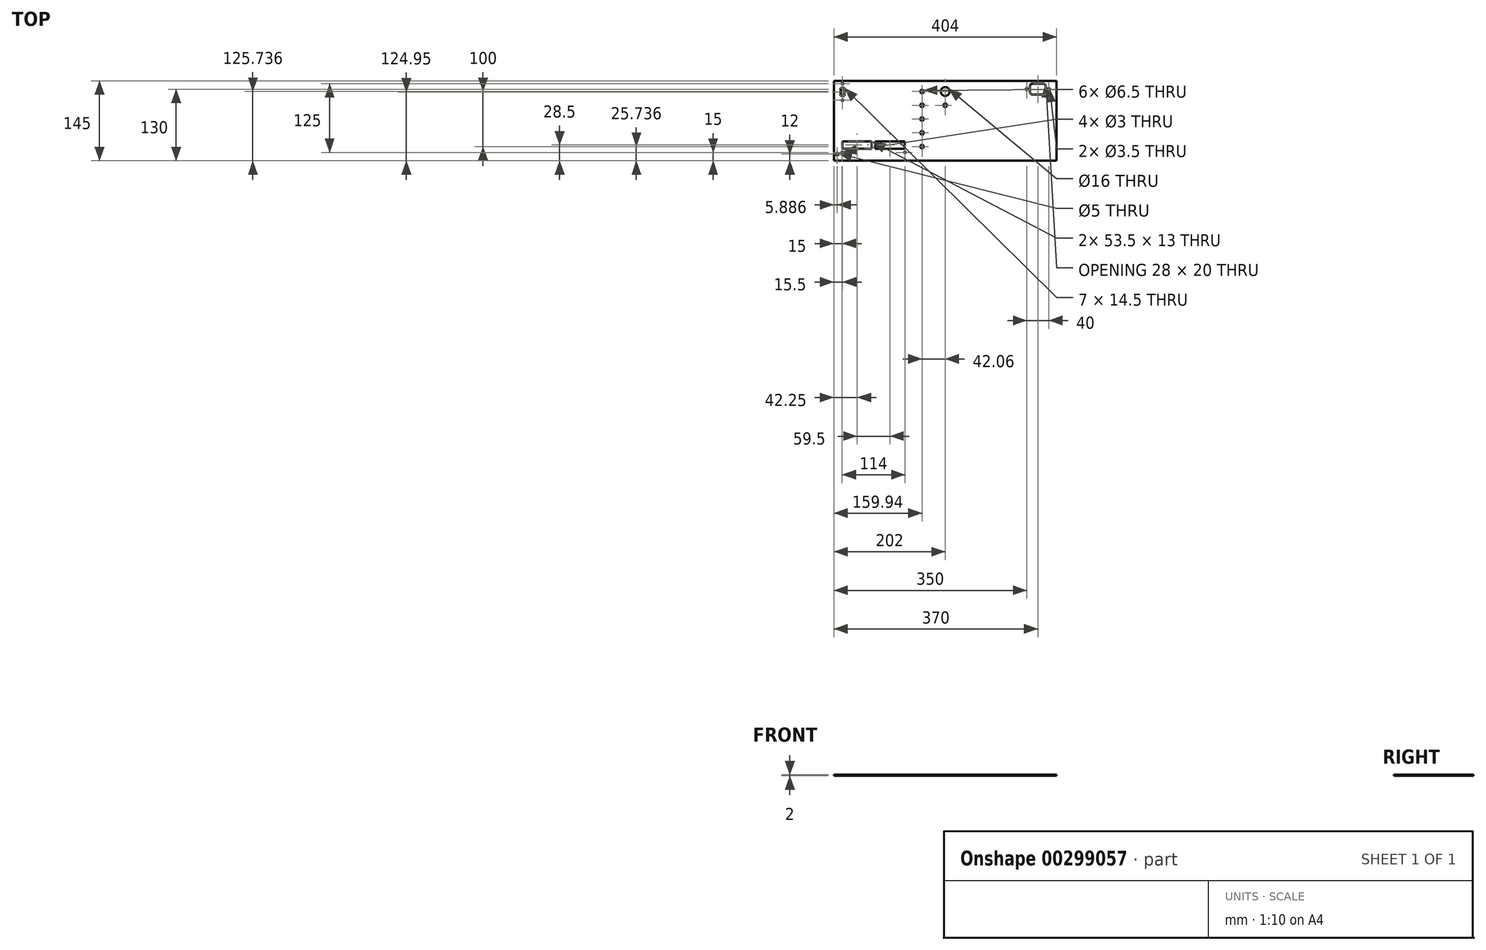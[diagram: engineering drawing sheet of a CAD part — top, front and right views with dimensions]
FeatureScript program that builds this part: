
annotation { "Feature Type Name" : "Feature", "Feature Type Description" : "" }
export const myFeature = defineFeature(function(context is Context, id is Id, definition is map)
    precondition{}
    {
        {
            var Q0;
            Q0=qCreatedBy(makeId("Top.planeOp"),FACE);
            var sketch = newSketch(context, id + "F0", { "sketchPlane" : qUnion([Q0])});
            skLineSegment(sketch, "E0.bottom", {"start": v(-202, 72.5) * mm, "end": v(202, 72.5) * mm});
            skLineSegment(sketch, "E0.top", {"start": v(-202, -72.5) * mm, "end": v(202, -72.5) * mm});
            skLineSegment(sketch, "E0.left", {"start": v(-202, 72.5) * mm, "end": v(-202, -72.5) * mm});
            skLineSegment(sketch, "E0.right", {"start": v(202, 72.5) * mm, "end": v(202, -72.5) * mm});
            skPoint(sketch, "E0.middle", {"position": v(0, 0) * mm});
            skLineSegment(sketch, "E1.bottom", {"start": v(-183, 45.2) * mm, "end": v(-190, 45.2) * mm});
            skLineSegment(sketch, "E1.top", {"start": v(-183, 59.7) * mm, "end": v(-190, 59.7) * mm});
            skLineSegment(sketch, "E1.left", {"start": v(-183, 45.2) * mm, "end": v(-183, 59.7) * mm});
            skLineSegment(sketch, "E1.right", {"start": v(-190, 45.2) * mm, "end": v(-190, 59.7) * mm});
            skPoint(sketch, "E1.middle", {"position": v(-186.5, 52.45) * mm});
            skCircle(sketch, "E2", {"center": v(-186.5, 67.5) * mm, "radius": 1.5 * mm});
            skCircle(sketch, "E3", {"center": v(-186.5, 37.4) * mm, "radius": 1.5 * mm});
            skLineSegment(sketch, "E4.bottom", {"start": v(178, 47.5) * mm, "end": v(158, 47.5) * mm});
            skLineSegment(sketch, "E4.top", {"start": v(178, 67.5) * mm, "end": v(158, 67.5) * mm});
            skLineSegment(sketch, "E4.left", {"start": v(182, 51.5) * mm, "end": v(182, 63.5) * mm});
            skLineSegment(sketch, "E4.right", {"start": v(154, 51.5) * mm, "end": v(154, 63.5) * mm});
            skPoint(sketch, "E4.middle", {"position": v(168, 57.5) * mm});
            skCircle(sketch, "E5", {"center": v(148, 57.5) * mm, "radius": 1.75 * mm});
            skCircle(sketch, "E6", {"center": v(188, 57.5) * mm, "radius": 1.75 * mm});
            skCircle(sketch, "E7", {"center": v(-42.06, 53.24) * mm, "radius": 3.25 * mm});
            skCircle(sketch, "E8", {"center": v(0, 28.24) * mm, "radius": 3.25 * mm});
            skCircle(sketch, "E9", {"center": v(0, 53.24) * mm, "radius": 8 * mm});
            skCircle(sketch, "E10.7.4.0", {"center": v(-196.11, -60.5) * mm, "radius": 2.5 * mm});
            skLineSegment(sketch, "E11.bottom", {"start": v(-133, -50.5) * mm, "end": v(-186.5, -50.5) * mm});
            skLineSegment(sketch, "E11.top", {"start": v(-133, -37.5) * mm, "end": v(-186.5, -37.5) * mm});
            skLineSegment(sketch, "E11.left", {"start": v(-133, -50.5) * mm, "end": v(-133, -37.5) * mm});
            skLineSegment(sketch, "E11.right", {"start": v(-186.5, -50.5) * mm, "end": v(-186.5, -37.5) * mm});
            skPoint(sketch, "E11.middle", {"position": v(-159.75, -44) * mm});
            skLineSegment(sketch, "E12.bottom", {"start": v(-73.5, -50.5) * mm, "end": v(-127, -50.5) * mm});
            skLineSegment(sketch, "E12.top", {"start": v(-73.5, -37.5) * mm, "end": v(-127, -37.5) * mm});
            skLineSegment(sketch, "E12.left", {"start": v(-73.5, -50.5) * mm, "end": v(-73.5, -37.5) * mm});
            skLineSegment(sketch, "E12.right", {"start": v(-127, -50.5) * mm, "end": v(-127, -37.5) * mm});
            skPoint(sketch, "E12.middle", {"position": v(-100.25, -44) * mm});
            skCircle(sketch, "E13.0.1.0", {"center": v(-42.06, 28.24) * mm, "radius": 3.25 * mm});
            skCircle(sketch, "E13.0.2.0", {"center": v(-42.06, 3.24) * mm, "radius": 3.25 * mm});
            skCircle(sketch, "E13.0.3.0", {"center": v(-42.06, -21.76) * mm, "radius": 3.25 * mm});
            skCircle(sketch, "E13.0.4.0", {"center": v(-42.06, -46.76) * mm, "radius": 3.25 * mm});
            skLineSegment(sketch, "E13.direction1", {"start": v(-42.06, 53.24) * mm, "end": v(-17.64, 53.24) * mm, "construction": true});
            skLineSegment(sketch, "E13.direction2", {"start": v(-42.06, 53.24) * mm, "end": v(-42.06, 28.24) * mm, "construction": true});
            skPoint(sketch, "E14.visualSharp", {"position": v(154, 67.5) * mm});
            skArc(sketch, "E14.filletArc", {"start": v(158, 67.5) * mm, "mid": v(155.17, 66.33) * mm, "end": v(154, 63.5) * mm});
            skPoint(sketch, "E15.visualSharp", {"position": v(182, 67.5) * mm});
            skArc(sketch, "E15.filletArc", {"start": v(182, 63.5) * mm, "mid": v(180.83, 66.33) * mm, "end": v(178, 67.5) * mm});
            skPoint(sketch, "E16.visualSharp", {"position": v(182, 47.5) * mm});
            skArc(sketch, "E16.filletArc", {"start": v(178, 47.5) * mm, "mid": v(180.83, 48.67) * mm, "end": v(182, 51.5) * mm});
            skPoint(sketch, "E17.visualSharp", {"position": v(154, 47.5) * mm});
            skArc(sketch, "E17.filletArc", {"start": v(154, 51.5) * mm, "mid": v(155.17, 48.67) * mm, "end": v(158, 47.5) * mm});
            skLineSegment(sketch, "E18", {"start": v(-190, 19.5) * mm, "end": v(-190, -60.5) * mm, "construction": true});
            skLineSegment(sketch, "E19", {"start": v(-70, -60.5) * mm, "end": v(-70, 19.5) * mm, "construction": true});
            skLineSegment(sketch, "E20", {"start": v(27, 37.5) * mm, "end": v(27, -72.5) * mm, "construction": true});
            skLineSegment(sketch, "E21", {"start": v(27, -72.5) * mm, "end": v(197, -72.5) * mm, "construction": true});
            skLineSegment(sketch, "E22", {"start": v(197, -72.5) * mm, "end": v(197, 37.5) * mm, "construction": true});
            skLineSegment(sketch, "E23", {"start": v(197, 37.5) * mm, "end": v(27, 37.5) * mm, "construction": true});
            skLineSegment(sketch, "E24", {"start": v(-190, -60.5) * mm, "end": v(-70, -60.5) * mm, "construction": true});
            skLineSegment(sketch, "E25", {"start": v(-190, 19.5) * mm, "end": v(-70, 19.5) * mm, "construction": true});
            skCircle(sketch, "E26", {"center": v(-187, -57.5) * mm, "radius": 1.5 * mm});
            skCircle(sketch, "E27", {"center": v(-73, -57.5) * mm, "radius": 1.5 * mm});
            skSolve(sketch);
        }
        {
            var Q0;
            Q0 = qSketchRegion(id + "F0", true);
            extrude(context, id + "F1", {"entities" : qUnion([Q0]), "oppositeDirection" : true, "depth" : 2 * mm});
        }
    });
